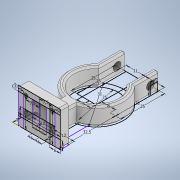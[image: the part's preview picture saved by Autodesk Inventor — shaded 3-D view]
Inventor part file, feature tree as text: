
AUTODESK INVENTOR PART (.ipt)
format: ipt  version: 2020 (Build 240168000, 168)  size: 263,680 bytes
history: native  units: mm
features: sketch x3, extrude x3, hole x2, fillet x1, chamfer x1
ambient origin geometry x8: Origin, YZ Plane, XZ Plane, XY Plane, X Axis, Y Axis, Z Axis, Center Point
bodies: Volumenkörper1 (feature_tree), Volumenkörper2 (feature_tree)
feature tree (10):
  sketch  "Skizze1"  dims[d0=25.0mm d1=8.0mm]
  extrude  "Extrusion1"  Depth=8.0mm
  extrude  "Extrusion2"  Depth=8.0mm
  sketch  "Skizze2"  dims[d2=25.0mm d3=8.0mm]
  extrude  "Extrusion3"  Depth=10.0mm
  fillet  "Rundung1"  Radius=5.0mm
  chamfer  "Fase1"  Distance=12.0mm
  sketch  "Skizze3"  dims[d4=25.0mm d5=32.5mm d6=5.0mm d7=12.0mm d8=12.0mm d9=5.0mm d10=31.0mm d11=11.0mm d12=25.0mm d13=11.0mm d14=25.0mm d15=4.0mm d16=4.0mm d17=10.0mm d18=0.0mm d19=20.0mm d20=0.0mm d21=24.0mm d22=5.0mm d24=3.0mm d25=17.0mm d26=3.0mm d27=17.0mm d35=6.0mm d36=3.0mm d37=4.0mm d38=4.0mm d39=3.0mm d40=0.0mm d41=5.0mm d42=2.0mm d43=1.0mm d44=2.0mm d45=45.0deg d46=4.0mm d47=5.0mm d48=4.5mm d49=8.0mm d50=9.4mm d51=2.0mm d52=90.0deg d53=11.8mm d54=20.594885mm d55=7.5mm d56=7.5mm d57=2.459mm d58=6.0mm d59=6.3mm d60=2.0mm d61=90.0deg d62=8.8mm d63=20.594885mm]
  hole  "Bohrung2"  [1 undecoded]
  hole  "Bohrung3"  [1 undecoded]
note: 2 required parameter values undecoded (feature->parameter linkage not recoverable at this tier; creation-order binding heuristic only, values carry confidence <= 0.55)
